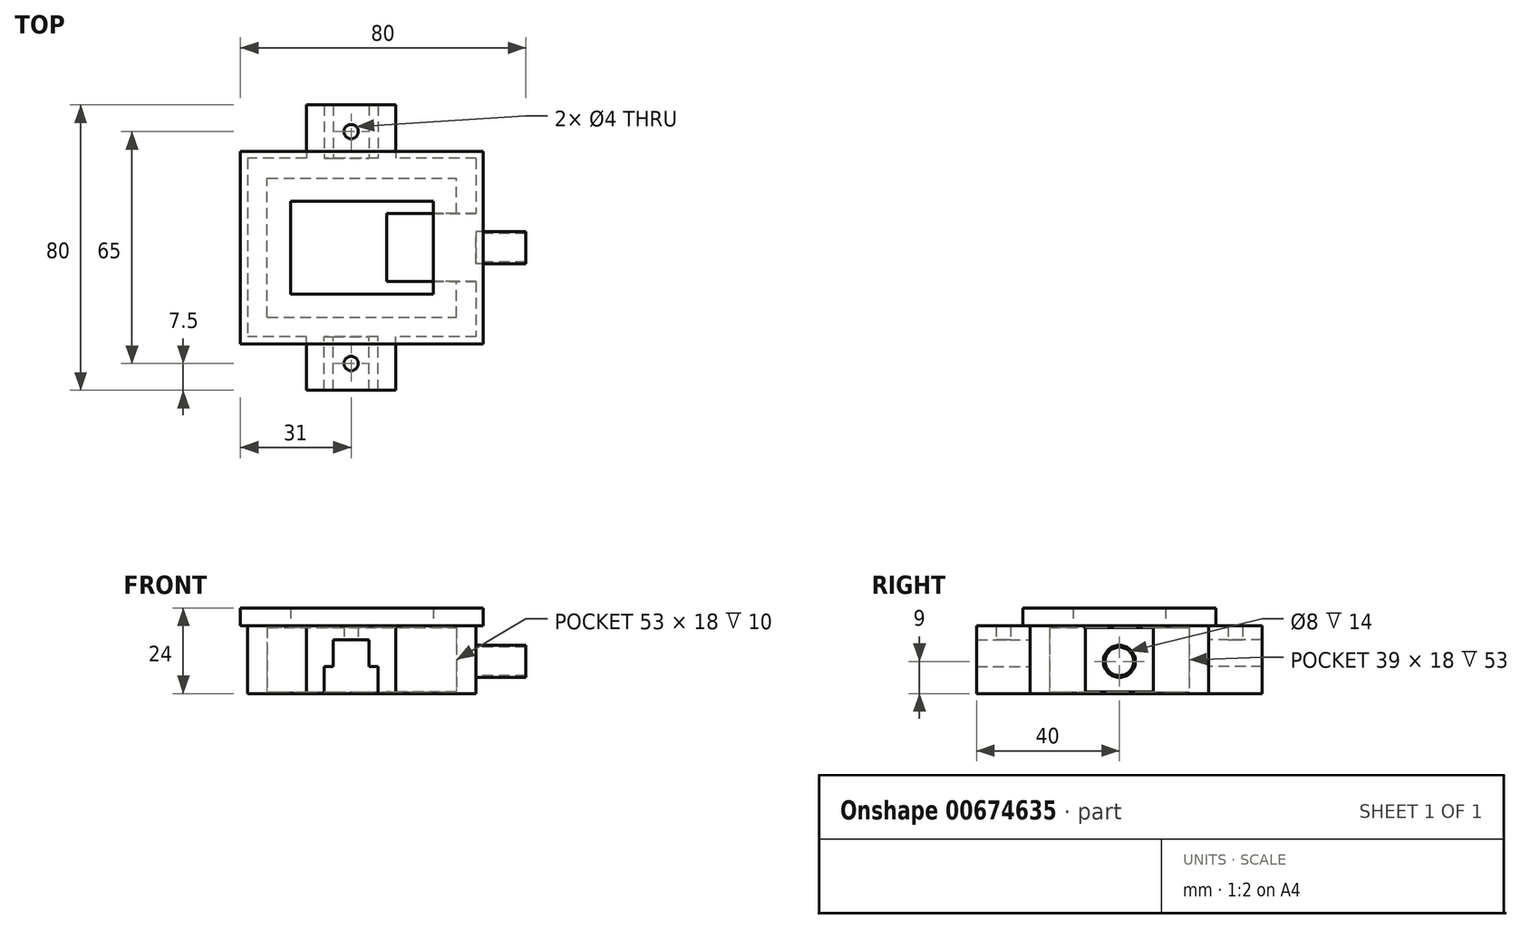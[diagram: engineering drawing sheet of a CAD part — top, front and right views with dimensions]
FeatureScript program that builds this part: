
annotation { "Feature Type Name" : "Feature", "Feature Type Description" : "" }
export const myFeature = defineFeature(function(context is Context, id is Id, definition is map)
    precondition{}
    {
        {
            var Q0;
            Q0=qCreatedBy(makeId("Front.planeOp"),FACE);
            var sketch = newSketch(context, id + "F0", { "sketchPlane" : qUnion([Q0])});
            skLineSegment(sketch, "E0", {"start": v(-24, 19) * mm, "end": v(30, 19) * mm});
            skLineSegment(sketch, "E1", {"start": v(-24, 19) * mm, "end": v(-24, 0) * mm});
            skLineSegment(sketch, "E2", {"start": v(-24, 0) * mm, "end": v(30, 0) * mm});
            skLineSegment(sketch, "E3", {"start": v(30, 0) * mm, "end": v(30, 19) * mm});
            skPoint(sketch, "E4", {"position": v(0, 0) * mm});
            skSolve(sketch);
        }
        {
            var Q0;
            Q0=makeQuery(id+"F0.imprint","IMPRINT",FACE,{"disambiguationData":[TD([[makeQuery(id+"F0.imprint","IMPRINT",EDGE,{"derivedFrom":sQuery(id+"F0.wireOp",EDGE,"E0")}),-1.0]])]});
            extrude(context, id + "F1", {"entities" : qUnion([Q0]), "depth" : 40 * mm, "offsetDistance" : 25 * mm, "symmetric" : true});
        }
        {
            var Q0;
            Q0=makeQuery(id+"F1.opExtrude","SWEPT_FACE",FACE,{"disambiguationData":[OSD([sQuery(id+"F0.wireOp",EDGE,"E3")])]});
            var sketch = newSketch(context, id + "F2", { "sketchPlane" : qUnion([Q0])});
            skLineSegment(sketch, "E5", {"start": v(-8.5, 0.5) * mm, "end": v(0, 0.5) * mm});
            skLineSegment(sketch, "E6", {"start": v(-8.5, 0.5) * mm, "end": v(-8.5, 17.5) * mm});
            skLineSegment(sketch, "E7", {"start": v(-8.5, 17.5) * mm, "end": v(0, 17.5) * mm});
            skLineSegment(sketch, "E8.MirrorCS", {"start": v(8.5, 17.5) * mm, "end": v(0, 17.5) * mm});
            skLineSegment(sketch, "E9.MirrorCS", {"start": v(8.5, 0.5) * mm, "end": v(8.5, 17.5) * mm});
            skLineSegment(sketch, "E10.MirrorCS", {"start": v(8.5, 0.5) * mm, "end": v(0, 0.5) * mm});
            skCircle(sketch, "E11", {"center": v(0, 9) * mm, "radius": 4.5 * mm});
            skPoint(sketch, "E12", {"position": v(-8.5, 9) * mm});
            skLineSegment(sketch, "E13", {"start": v(-8.5, 9) * mm, "end": v(8.5, 9) * mm, "construction": true});
            skSolve(sketch);
        }
        {
            var Q0;
            Q0=makeQuery(id+"F2.imprint","IMPRINT",FACE,{"disambiguationData":[TD([[makeQuery(id+"F2.imprint","IMPRINT",EDGE,{"derivedFrom":sQuery(id+"F2.wireOp",EDGE,"E5")}),1.0]])]});
            extrude(context, id + "F3", {"entities" : qUnion([Q0]), "operationType" : NewBodyOperationType.ADD, "depth" : 1.5 * mm, "offsetDistance" : 25 * mm});
        }
        {
            var Q0;
            Q0=makeQuery(id+"F3.boolean.opBoolean","SPLIT",FACE,{"disambiguationData":[TD([makeQuery(id+"F3.opExtrude","SWEPT_FACE",FACE,{"disambiguationData":[OSD([sQuery(id+"F2.wireOp",EDGE,"E11")])]})])],"derivedFrom":makeQuery(id+"F1.opExtrude","SWEPT_FACE",FACE,{"disambiguationData":[OSD([sQuery(id+"F0.wireOp",EDGE,"E3")])]})});
            extrude(context, id + "F4", {"entities" : qUnion([Q0]), "operationType" : NewBodyOperationType.ADD, "depth" : 19 * mm, "offsetDistance" : 25 * mm});
        }
        {
            var Q0;
            Q0=makeQuery(id+"F4.opExtrude","CAP_FACE",FACE,{"disambiguationData":[OSD([sQuery(id+"F0.wireOp",EDGE,"E3")])],"isStart":false});
            shell(context, id + "F5", {"entities" : qUnion([Q0]), "thickness" : .5 * mm});
        }
        {
            var Q0;
            Q0=makeQuery(id+"F1.opExtrude","SWEPT_FACE",FACE,{"disambiguationData":[OSD([sQuery(id+"F0.wireOp",EDGE,"E0")])]});
            var sketch = newSketch(context, id + "F6", { "sketchPlane" : qUnion([Q0])});
            skLineSegment(sketch, "E14.0", {"start": v(-29, 25) * mm, "end": v(35, 25) * mm});
            skLineSegment(sketch, "E14.1", {"start": v(-29, -25) * mm, "end": v(-29, 25) * mm});
            skLineSegment(sketch, "E15.0", {"start": v(35, -25) * mm, "end": v(35, 25) * mm});
            skLineSegment(sketch, "E15.1", {"start": v(-29, -25) * mm, "end": v(35, -25) * mm});
            skSolve(sketch);
        }
        {
            var Q0;
            Q0=makeQuery(id+"F6.imprint","IMPRINT",FACE,{"disambiguationData":[TD([[makeQuery(id+"F6.imprint","IMPRINT",EDGE,{"derivedFrom":sQuery(id+"F6.wireOp",EDGE,"E14.0")}),-1.0]])]});
            var Q1;
            Q1=qCreatedBy(makeId("Top.planeOp"),FACE);
            extrude(context, id + "F7", {"entities" : qUnion([Q0]), "endBound" : BoundingType.UP_TO_SURFACE, "oppositeDirection" : true, "depth" : 25 * mm, "endBoundEntityFace" : qUnion([Q1]), "offsetDistance" : 25 * mm});
        }
        {
            var Q0;
            Q0=makeQuery(id+"F7.opExtrude","SWEPT_FACE",FACE,{"disambiguationData":[OSD([sQuery(id+"F6.wireOp",EDGE,"E15.0")])]});
            var sketch = newSketch(context, id + "F8", { "sketchPlane" : qUnion([Q0])});
            skLineSegment(sketch, "E16.0", {"start": v(9.5, -0.5) * mm, "end": v(0, -0.5) * mm});
            skLineSegment(sketch, "E16.1", {"start": v(9.5, 19) * mm, "end": v(0, 19) * mm});
            skLineSegment(sketch, "E16.2", {"start": v(-9.5, 19) * mm, "end": v(0, 19) * mm});
            skLineSegment(sketch, "E16.3", {"start": v(9.5, -0.5) * mm, "end": v(9.5, 19) * mm});
            skLineSegment(sketch, "E16.4", {"start": v(-9.5, -0.5) * mm, "end": v(-9.5, 19) * mm});
            skLineSegment(sketch, "E16.5", {"start": v(-9.5, -0.5) * mm, "end": v(0, -0.5) * mm});
            skSolve(sketch);
        }
        {
            var Q0;
            Q0=qSketchRegion(id+"F8",true);
            var Q1;
            Q1=makeQuery(id+"F7.opExtrude","SWEPT_FACE",FACE,{"disambiguationData":[OSD([sQuery(id+"F6.wireOp",EDGE,"E15.0")])]});
            var Q2;
            Q2=makeQuery(id+"F1.opExtrude","SWEPT_BODY",BODY,{"disambiguationData":[OSD([sQuery(id+"F0.wireOp",EDGE,"E0"),sQuery(id+"F0.wireOp",EDGE,"E1"),sQuery(id+"F0.wireOp",EDGE,"E2"),sQuery(id+"F0.wireOp",EDGE,"E3")])]});
            extrude(context, id + "F9", {"entities" : qUnion([Q0]), "operationType" : NewBodyOperationType.REMOVE, "oppositeDirection" : true, "depth" : 25 * mm, "endBoundEntityFace" : qUnion([Q1]), "endBoundEntityBody" : qUnion([Q2]), "offsetDistance" : 25 * mm});
        }
        {
            var Q0;
            Q0=makeQuery(id+"F7.opExtrude","SWEPT_FACE",FACE,{"disambiguationData":[OSD([sQuery(id+"F6.wireOp",EDGE,"E14.1")])]});
            var sketch = newSketch(context, id + "F10", { "sketchPlane" : qUnion([Q0])});
            skLineSegment(sketch, "E17", {"start": v(-22, 19) * mm, "end": v(-22, 22.1) * mm});
            skLineSegment(sketch, "E18", {"start": v(0, 19) * mm, "end": v(0, 0) * mm, "construction": true});
            skLineSegment(sketch, "E19", {"start": v(-22, 22.1) * mm, "end": v(0, 22.1) * mm});
            skLineSegment(sketch, "E20", {"start": v(-22, 19) * mm, "end": v(0, 19) * mm});
            skLineSegment(sketch, "E21.MirrorCS", {"start": v(22, 22.1) * mm, "end": v(0, 22.1) * mm});
            skLineSegment(sketch, "E22.MirrorCS", {"start": v(22, 19) * mm, "end": v(22, 22.1) * mm});
            skLineSegment(sketch, "E23.MirrorCS", {"start": v(22, 19) * mm, "end": v(0, 19) * mm});
            skLineSegment(sketch, "E24", {"start": v(-22, 19.1) * mm, "end": v(0, 19.1) * mm});
            skLineSegment(sketch, "E25.MirrorCS", {"start": v(22, 19.1) * mm, "end": v(0, 19.1) * mm});
            skSolve(sketch);
        }
        {
            var Q0;
            Q0=makeQuery(id+"F6.imprint","IMPRINT",FACE,{"disambiguationData":[TD([[makeQuery(id+"F6.imprint","IMPRINT",EDGE,{"derivedFrom":sQuery(id+"F6.wireOp",EDGE,"E14.0")}),-1.0]])]});
            var sketch = newSketch(context, id + "F11", { "sketchPlane" : qUnion([Q0])});
            skLineSegment(sketch, "E26.0", {"start": v(-31, 27) * mm, "end": v(37, 27) * mm});
            skLineSegment(sketch, "E26.1", {"start": v(-31, -27) * mm, "end": v(-31, 27) * mm});
            skLineSegment(sketch, "E26.2", {"start": v(-31, -27) * mm, "end": v(37, -27) * mm});
            skLineSegment(sketch, "E26.3", {"start": v(37, -27) * mm, "end": v(37, 27) * mm});
            skLineSegment(sketch, "E27.0", {"start": v(23, 13) * mm, "end": v(-17, 13) * mm});
            skLineSegment(sketch, "E27.1", {"start": v(23, -13) * mm, "end": v(23, 13) * mm});
            skLineSegment(sketch, "E27.2", {"start": v(-17, -13) * mm, "end": v(23, -13) * mm});
            skLineSegment(sketch, "E27.3", {"start": v(-17, 13) * mm, "end": v(-17, -13) * mm});
            skLineSegment(sketch, "E28", {"start": v(3, 27) * mm, "end": v(3, 20) * mm, "construction": true});
            skPoint(sketch, "E29", {"position": v(3, 25) * mm});
            skLineSegment(sketch, "E30", {"start": v(3, 25) * mm, "end": v(3, 20) * mm, "construction": true});
            skLineSegment(sketch, "E31", {"start": v(3, 22.5) * mm, "end": v(-7, 22.5) * mm, "construction": true});
            skLineSegment(sketch, "E32", {"start": v(-7, 22.5) * mm, "end": v(-7, 23.5) * mm});
            skLineSegment(sketch, "E33", {"start": v(-7, 23.5) * mm, "end": v(3, 23.5) * mm});
            skLineSegment(sketch, "E34.MirrorCS", {"start": v(-7, 21.5) * mm, "end": v(3, 21.5) * mm});
            skLineSegment(sketch, "E35.MirrorCS", {"start": v(-7, 22.5) * mm, "end": v(-7, 21.5) * mm});
            skLineSegment(sketch, "E36.MirrorCS", {"start": v(13, 23.5) * mm, "end": v(3, 23.5) * mm});
            skLineSegment(sketch, "E37.MirrorCS", {"start": v(13, 22.5) * mm, "end": v(13, 23.5) * mm});
            skLineSegment(sketch, "E38.MirrorCS", {"start": v(13, 21.5) * mm, "end": v(3, 21.5) * mm});
            skLineSegment(sketch, "E39.MirrorCS", {"start": v(13, 22.5) * mm, "end": v(13, 21.5) * mm});
            skLineSegment(sketch, "E40.0", {"start": v(-7.05, 22.5) * mm, "end": v(-7.05, 23.55) * mm});
            skLineSegment(sketch, "E40.1", {"start": v(-7.05, 22.5) * mm, "end": v(-7.05, 21.45) * mm});
            skLineSegment(sketch, "E40.2", {"start": v(-7.05, 23.55) * mm, "end": v(3, 23.55) * mm});
            skLineSegment(sketch, "E40.3", {"start": v(-7.05, 21.45) * mm, "end": v(3, 21.45) * mm});
            skLineSegment(sketch, "E40.4", {"start": v(13.05, 23.55) * mm, "end": v(3, 23.55) * mm});
            skLineSegment(sketch, "E40.5", {"start": v(13.05, 22.5) * mm, "end": v(13.05, 23.55) * mm});
            skLineSegment(sketch, "E40.6", {"start": v(13.05, 22.5) * mm, "end": v(13.05, 21.45) * mm});
            skLineSegment(sketch, "E40.7", {"start": v(13.05, 21.45) * mm, "end": v(3, 21.45) * mm});
            skLineSegment(sketch, "E41", {"start": v(-31, 0) * mm, "end": v(37, 0) * mm, "construction": true});
            skLineSegment(sketch, "E42.MirrorCS", {"start": v(-7, -22.5) * mm, "end": v(-7, -23.5) * mm});
            skLineSegment(sketch, "E43.MirrorCS", {"start": v(-7, -22.5) * mm, "end": v(-7, -21.5) * mm});
            skLineSegment(sketch, "E44.MirrorCS", {"start": v(-7, -21.5) * mm, "end": v(3, -21.5) * mm});
            skLineSegment(sketch, "E45.MirrorCS", {"start": v(-7, -23.5) * mm, "end": v(3, -23.5) * mm});
            skLineSegment(sketch, "E46.MirrorCS", {"start": v(13, -23.5) * mm, "end": v(3, -23.5) * mm});
            skLineSegment(sketch, "E47.MirrorCS", {"start": v(13, -21.5) * mm, "end": v(3, -21.5) * mm});
            skLineSegment(sketch, "E48.MirrorCS", {"start": v(13, -22.5) * mm, "end": v(13, -23.5) * mm});
            skLineSegment(sketch, "E49.MirrorCS", {"start": v(13, -22.5) * mm, "end": v(13, -21.5) * mm});
            skLineSegment(sketch, "E50.0", {"start": v(13.05, -22.5) * mm, "end": v(13.05, -23.55) * mm});
            skLineSegment(sketch, "E50.1", {"start": v(13.05, -22.5) * mm, "end": v(13.05, -21.45) * mm});
            skLineSegment(sketch, "E50.2", {"start": v(13.05, -23.55) * mm, "end": v(3, -23.55) * mm});
            skLineSegment(sketch, "E50.3", {"start": v(13.05, -21.45) * mm, "end": v(3, -21.45) * mm});
            skLineSegment(sketch, "E50.4", {"start": v(-7.05, -23.55) * mm, "end": v(3, -23.55) * mm});
            skLineSegment(sketch, "E50.5", {"start": v(-7.05, -22.5) * mm, "end": v(-7.05, -23.55) * mm});
            skLineSegment(sketch, "E50.6", {"start": v(-7.05, -22.5) * mm, "end": v(-7.05, -21.45) * mm});
            skLineSegment(sketch, "E50.7", {"start": v(-7.05, -21.45) * mm, "end": v(3, -21.45) * mm});
            skLineSegment(sketch, "E51", {"start": v(-31, -27) * mm, "end": v(-29.4, -25.4) * mm, "construction": true});
            skLineSegment(sketch, "E52", {"start": v(-31, 0) * mm, "end": v(-24.69, 0) * mm, "construction": true});
            skPoint(sketch, "E53", {"position": v(-29, 0) * mm});
            skLineSegment(sketch, "E54", {"start": v(-29, 0) * mm, "end": v(-24.69, 0) * mm, "construction": true});
            skLineSegment(sketch, "E55", {"start": v(-26.84, 0) * mm, "end": v(-26.84, -10) * mm, "construction": true});
            skLineSegment(sketch, "E56", {"start": v(-26.84, -10) * mm, "end": v(-27.9, -10) * mm});
            skLineSegment(sketch, "E57", {"start": v(-27.9, -10) * mm, "end": v(-27.9, 0) * mm});
            skLineSegment(sketch, "E58.MirrorCS", {"start": v(-25.78, -10) * mm, "end": v(-25.78, 0) * mm});
            skLineSegment(sketch, "E59.MirrorCS", {"start": v(-26.84, -10) * mm, "end": v(-25.78, -10) * mm});
            skLineSegment(sketch, "E60.MirrorCS", {"start": v(-27.9, 10) * mm, "end": v(-27.9, 0) * mm});
            skLineSegment(sketch, "E61.MirrorCS", {"start": v(-25.78, 10) * mm, "end": v(-25.78, 0) * mm});
            skLineSegment(sketch, "E62.MirrorCS", {"start": v(-26.84, 10) * mm, "end": v(-25.78, 10) * mm});
            skLineSegment(sketch, "E63.MirrorCS", {"start": v(-26.84, 10) * mm, "end": v(-27.9, 10) * mm});
            skSolve(sketch);
        }
        {
            var Q0;
            Q0=makeQuery(id+"F11.imprint","IMPRINT",FACE,{"disambiguationData":[TD([[makeQuery(id+"F11.imprint","IMPRINT",EDGE,{"derivedFrom":sQuery(id+"F11.wireOp",EDGE,"E26.0")}),-1.0]])]});
            var Q1;
            Q1=makeQuery(id+"F6.imprint","IMPRINT",FACE,{"disambiguationData":[TD([[makeQuery(id+"F6.imprint","IMPRINT",EDGE,{"derivedFrom":sQuery(id+"F6.wireOp",EDGE,"E14.0")}),-1.0]])]});
            var Q2;
            Q2=makeQuery(id+"F11.imprint","IMPRINT",FACE,{"disambiguationData":[TD([[makeQuery(id+"F11.imprint","IMPRINT",EDGE,{"derivedFrom":sQuery(id+"F11.wireOp",EDGE,"E27.0")}),-1.0]])]});
            var Q3;
            Q3=sQuery(id+"F11.wireOp",EDGE,"E26.1");
            var Q4;
            Q4=sQuery(id+"F11.wireOp",EDGE,"E26.2");
            var Q5;
            Q5=sQuery(id+"F11.wireOp",EDGE,"E26.3");
            var Q6;
            Q6=sQuery(id+"F11.wireOp",EDGE,"E26.0");
            var Q7;
            Q7=sQuery(id+"F11.wireOp",EDGE,"E27.0");
            var Q8;
            Q8=sQuery(id+"F11.wireOp",EDGE,"E27.1");
            var Q9;
            Q9=sQuery(id+"F11.wireOp",EDGE,"E27.2");
            var Q10;
            Q10=sQuery(id+"F11.wireOp",EDGE,"E27.3");
            extrude(context, id + "F12", {"entities" : qUnion([Q0, Q1, Q2]), "surfaceEntities" : qUnion([Q3, Q4, Q5, Q6, Q7, Q8, Q9, Q10]), "depth" : 5 * mm, "offsetDistance" : 25 * mm});
        }
        {
            var Q0;
            Q0=makeQuery(id+"F7.opExtrude","SWEPT_FACE",FACE,{"disambiguationData":[OSD([sQuery(id+"F6.wireOp",EDGE,"E14.0")])]});
            var sketch = newSketch(context, id + "F13", { "sketchPlane" : qUnion([Q0])});
            skLineSegment(sketch, "E64", {"start": v(0, 15) * mm, "end": v(-5, 15) * mm});
            skLineSegment(sketch, "E65", {"start": v(-5, 15) * mm, "end": v(-5, 0) * mm});
            skLineSegment(sketch, "E66", {"start": v(0, 19) * mm, "end": v(0, 0) * mm, "construction": true});
            skLineSegment(sketch, "E67.MirrorCS", {"start": v(0, 15) * mm, "end": v(5, 15) * mm});
            skLineSegment(sketch, "E68.MirrorCS", {"start": v(5, 15) * mm, "end": v(5, 0) * mm});
            skLineSegment(sketch, "E69", {"start": v(-5, 7.5) * mm, "end": v(-7.5, 7.5) * mm});
            skLineSegment(sketch, "E70", {"start": v(-7.5, 7.5) * mm, "end": v(-7.5, 0) * mm});
            skLineSegment(sketch, "E71.MirrorCS", {"start": v(5, 7.5) * mm, "end": v(7.5, 7.5) * mm});
            skLineSegment(sketch, "E72.MirrorCS", {"start": v(7.5, 7.5) * mm, "end": v(7.5, 0) * mm});
            skLineSegment(sketch, "E73", {"start": v(0, 19) * mm, "end": v(-12.5, 19) * mm});
            skLineSegment(sketch, "E74", {"start": v(-12.5, 19) * mm, "end": v(-12.5, 0) * mm});
            skLineSegment(sketch, "E75.MirrorCS", {"start": v(0, 19) * mm, "end": v(12.5, 19) * mm});
            skLineSegment(sketch, "E76.MirrorCS", {"start": v(12.5, 19) * mm, "end": v(12.5, 0) * mm});
            skLineSegment(sketch, "E77.0", {"start": v(-7.55, 7.6) * mm, "end": v(-7.55, 0) * mm});
            skLineSegment(sketch, "E78.0", {"start": v(0, 15.1) * mm, "end": v(-5.05, 15.1) * mm});
            skLineSegment(sketch, "E79", {"start": v(-5.05, 15.1) * mm, "end": v(-5.05, 7.6) * mm});
            skLineSegment(sketch, "E80", {"start": v(-7.55, 7.6) * mm, "end": v(-5.05, 7.6) * mm});
            skLineSegment(sketch, "E81.MirrorCS", {"start": v(0, 15.1) * mm, "end": v(5.05, 15.1) * mm});
            skLineSegment(sketch, "E82.MirrorCS", {"start": v(5.05, 15.1) * mm, "end": v(5.05, 7.6) * mm});
            skLineSegment(sketch, "E83.MirrorCS", {"start": v(7.55, 7.6) * mm, "end": v(5.05, 7.6) * mm});
            skLineSegment(sketch, "E84.MirrorCS", {"start": v(7.55, 7.6) * mm, "end": v(7.55, 0) * mm});
            skSolve(sketch);
        }
        {
            var Q0;
            Q0=qCreatedBy(makeId("Top.planeOp"),FACE);
            cPlane(context, id + "F14", {"entities" : qUnion([Q0]), "cplaneType" : CPlaneType.OFFSET, "offset" : 8 * mm, "oppositeDirection" : true, "width" : 150 * mm, "height" : 150 * mm});
        }
        {
            var Q0;
            Q0=makeQuery(id+"F13.imprint","IMPRINT",FACE,{"disambiguationData":[TD([[makeQuery(id+"F13.imprint","IMPRINT",EDGE,{"derivedFrom":sQuery(id+"F13.wireOp",EDGE,"E73")}),1.0]])]});
            extrude(context, id + "F15", {"entities" : qUnion([Q0]), "operationType" : NewBodyOperationType.ADD, "depth" : 15 * mm, "offsetDistance" : 25 * mm});
        }
        {
            var Q0;
            Q0=makeQuery(id+"F15.opExtrude","SWEPT_FACE",FACE,{"disambiguationData":[OSD([sQuery(id+"F13.wireOp",EDGE,"E78.0"),sQuery(id+"F13.wireOp",EDGE,"E81.MirrorCS")])]});
            var sketch = newSketch(context, id + "F16", { "sketchPlane" : qUnion([Q0])});
            skCircle(sketch, "E85.cCircle", {"center": v(0, -32.5) * mm, "radius": 3.5 * mm, "construction": true});
            skLineSegment(sketch, "E85.0", {"start": v(0, -29) * mm, "end": v(3.03, -30.75) * mm});
            skLineSegment(sketch, "E85.1", {"start": v(3.03, -30.75) * mm, "end": v(3.03, -34.25) * mm});
            skLineSegment(sketch, "E85.2", {"start": v(3.03, -34.25) * mm, "end": v(0, -36) * mm});
            skLineSegment(sketch, "E85.3", {"start": v(0, -36) * mm, "end": v(-3.03, -34.25) * mm});
            skLineSegment(sketch, "E85.4", {"start": v(-3.03, -34.25) * mm, "end": v(-3.03, -30.75) * mm});
            skLineSegment(sketch, "E85.5", {"start": v(-3.03, -30.75) * mm, "end": v(0, -29) * mm});
            skCircle(sketch, "E86", {"center": v(0, -32.5) * mm, "radius": 2 * mm});
            skLineSegment(sketch, "E87", {"start": v(0, -25) * mm, "end": v(0, -40) * mm, "construction": true});
            skSolve(sketch);
        }
        {
            var Q0;
            Q0=makeQuery(id+"F16.imprint","IMPRINT",FACE,{"disambiguationData":[TD([[makeQuery(id+"F16.imprint","IMPRINT",EDGE,{"derivedFrom":sQuery(id+"F16.wireOp",EDGE,"E86")}),1.0]])]});
            var Q1;
            Q1=sQuery(id+"F16.wireOp",EDGE,"E86");
            extrude(context, id + "F17", {"entities" : qUnion([Q0]), "operationType" : NewBodyOperationType.REMOVE, "surfaceEntities" : qUnion([Q1]), "endBound" : BoundingType.THROUGH_ALL, "oppositeDirection" : true, "depth" : 25 * mm, "offsetDistance" : 25 * mm});
        }
        {
            var Q0;
            Q0=makeQuery(id+"F7.opExtrude","SWEPT_BODY",BODY,{"disambiguationData":[OSD([sQuery(id+"F0.wireOp",EDGE,"E0"),sQuery(id+"F0.wireOp",EDGE,"E1"),sQuery(id+"F0.wireOp",EDGE,"E3"),sQuery(id+"F6.wireOp",EDGE,"E14.0"),sQuery(id+"F6.wireOp",EDGE,"E14.1"),sQuery(id+"F6.wireOp",EDGE,"E15.0"),sQuery(id+"F6.wireOp",EDGE,"E15.1")])]});
            var Q1;
            Q1=qCreatedBy(makeId("Front.planeOp"),FACE);
            mirror(context, id + "F18", {"operationType" : NewBodyOperationType.ADD, "entities" : qUnion([Q0]), "mirrorPlane" : qUnion([Q1])});
        }
    });
